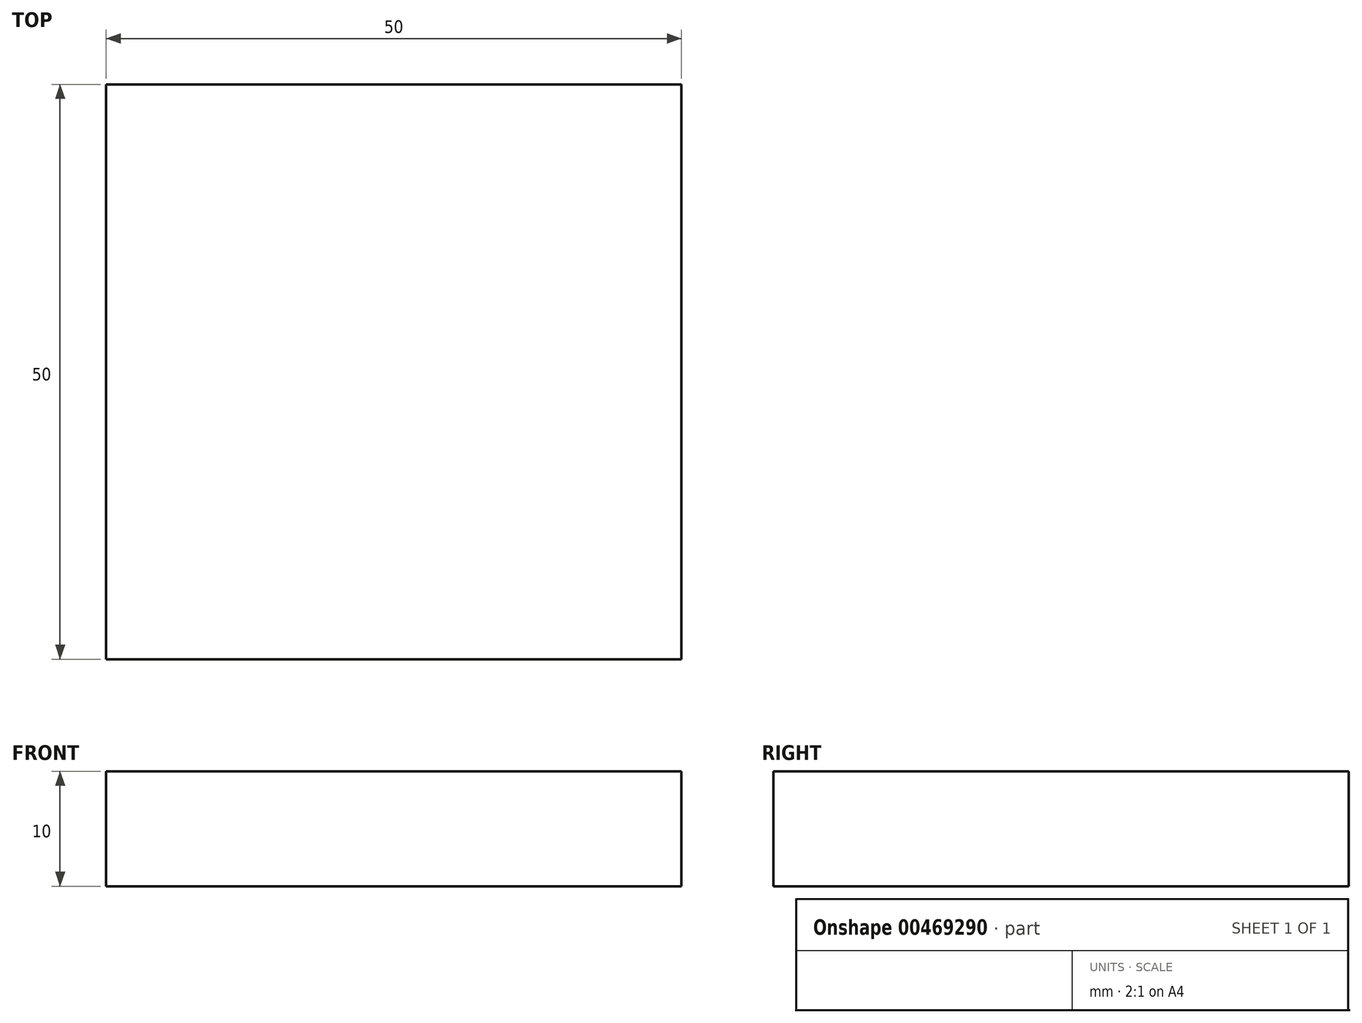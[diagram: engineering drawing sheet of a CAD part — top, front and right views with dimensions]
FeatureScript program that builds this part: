
annotation { "Feature Type Name" : "Feature", "Feature Type Description" : "" }
export const myFeature = defineFeature(function(context is Context, id is Id, definition is map)
    precondition{}
    {
        {
            var Q0;
            Q0=qCreatedBy(makeId("Top.planeOp"),FACE);
            var sketch = newSketch(context, id + "F0", { "sketchPlane" : qUnion([Q0])});
            skLineSegment(sketch, "E0.bottom", {"start": v(-25, 25) * mm, "end": v(25, 25) * mm});
            skLineSegment(sketch, "E0.top", {"start": v(-25, -25) * mm, "end": v(25, -25) * mm});
            skLineSegment(sketch, "E0.left", {"start": v(-25, 25) * mm, "end": v(-25, -25) * mm});
            skLineSegment(sketch, "E0.right", {"start": v(25, 25) * mm, "end": v(25, -25) * mm});
            skPoint(sketch, "E0.middle", {"position": v(0, 0) * mm});
            skSolve(sketch);
        }
        {
            var Q0;
            Q0=makeQuery(id+"F0.imprint","IMPRINT",FACE,{"disambiguationData":[TD([[makeQuery(id+"F0.imprint","IMPRINT",EDGE,{"derivedFrom":sQuery(id+"F0.wireOp",EDGE,"E0.bottom")}),-1.0]])]});
            extrude(context, id + "F1", {"entities" : qUnion([Q0]), "depth" : 10 * mm, "offsetDistance" : 25 * mm});
        }
    });
